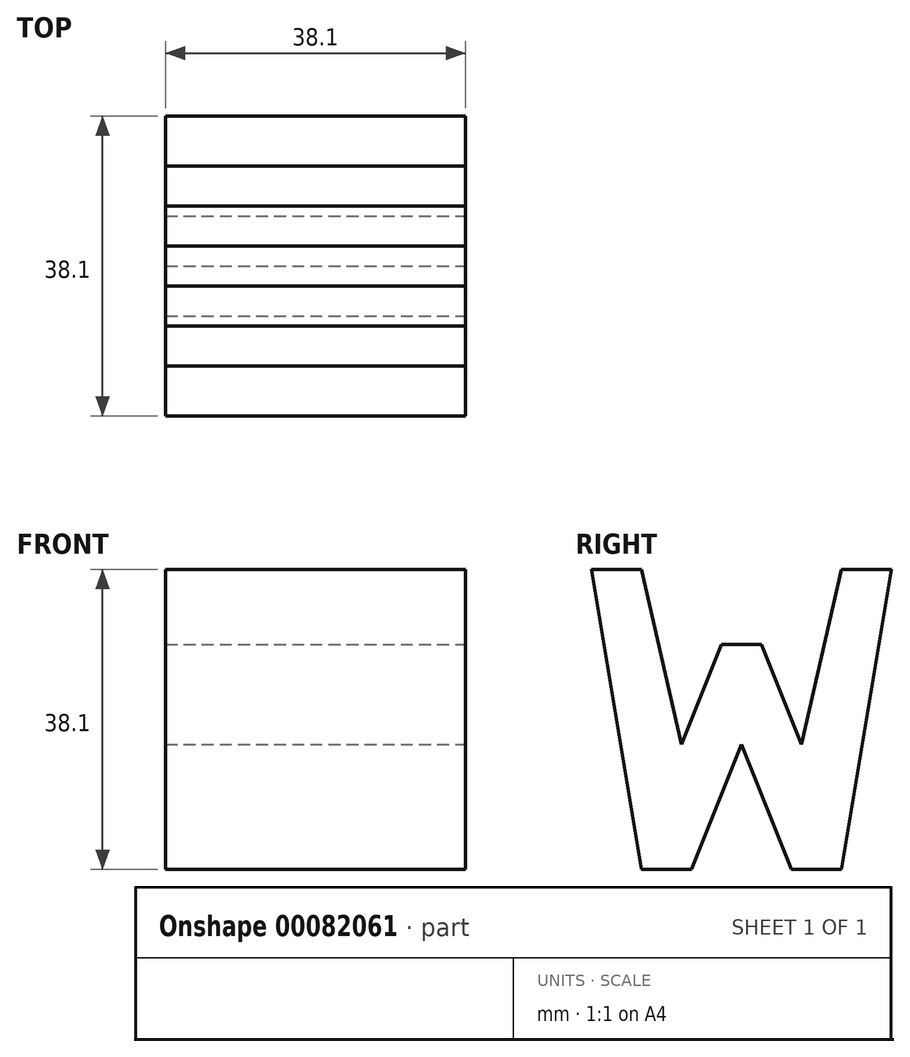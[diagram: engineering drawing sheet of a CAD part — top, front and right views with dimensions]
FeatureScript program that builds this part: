
annotation { "Feature Type Name" : "Feature", "Feature Type Description" : "" }
export const myFeature = defineFeature(function(context is Context, id is Id, definition is map)
    precondition{}
    {
        {
            var Q0;
            Q0=qCreatedBy(makeId("Front.planeOp"),FACE);
            var sketch = newSketch(context, id + "F0", { "sketchPlane" : qUnion([Q0])});
            skLineSegment(sketch, "E0", {"start": v(0, 0) * mm, "end": v(38.1, 0) * mm});
            skLineSegment(sketch, "E1", {"start": v(38.1, 0) * mm, "end": v(38.1, 38.1) * mm});
            skLineSegment(sketch, "E2", {"start": v(38.1, 38.1) * mm, "end": v(0, 38.1) * mm});
            skLineSegment(sketch, "E3", {"start": v(0, 0) * mm, "end": v(0, 38.1) * mm});
            skSolve(sketch);
        }
        {
            var Q0;
            Q0 = qSketchRegion(id + "F0", true);
            extrude(context, id + "F1", {"entities" : qUnion([Q0]), "depth" : 38.1 * mm});
        }
        {
            var Q0;
            Q0=qCreatedBy(makeId("Front.planeOp"),FACE);
            cPlane(context, id + "F2", {"entities" : qUnion([Q0]), "cplaneType" : CPlaneType.OFFSET, "offset" : 38.1 * mm, "width" : 152.4 * mm, "height" : 152.4 * mm});
        }
        {
            var Q0;
            Q0=qCreatedBy(makeId("Right.planeOp"),FACE);
            cPlane(context, id + "F3", {"entities" : qUnion([Q0]), "cplaneType" : CPlaneType.OFFSET, "offset" : 38.1 * mm, "width" : 152.4 * mm, "height" : 152.4 * mm});
        }
        {
            var Q0;
            Q0=qCreatedBy(id+"F3.planeOp",FACE);
            var sketch = newSketch(context, id + "F4", { "sketchPlane" : qUnion([Q0])});
            skLineSegment(sketch, "E4", {"start": v(0, 38.1) * mm, "end": v(-38.1, 38.1) * mm});
            skLineSegment(sketch, "E5", {"start": v(-38.1, 38.1) * mm, "end": v(-38.1, 0) * mm});
            skLineSegment(sketch, "E6", {"start": v(-38.1, 0) * mm, "end": v(0, 0) * mm});
            skLineSegment(sketch, "E7", {"start": v(-38.1, 38.1) * mm, "end": v(-31.75, 0) * mm});
            skLineSegment(sketch, "E8", {"start": v(-25.4, 0) * mm, "end": v(-19.05, 15.88) * mm});
            skLineSegment(sketch, "E9", {"start": v(-19.05, 15.88) * mm, "end": v(-12.7, 0) * mm});
            skLineSegment(sketch, "E10", {"start": v(-12.7, 0) * mm, "end": v(-6.35, 0) * mm});
            skLineSegment(sketch, "E11", {"start": v(-6.35, 0) * mm, "end": v(0, 38.1) * mm});
            skLineSegment(sketch, "E12", {"start": v(-31.75, 38.1) * mm, "end": v(-26.67, 15.88) * mm});
            skLineSegment(sketch, "E13", {"start": v(-26.67, 15.88) * mm, "end": v(-21.59, 28.58) * mm});
            skLineSegment(sketch, "E14", {"start": v(-21.59, 28.58) * mm, "end": v(-16.5, 28.58) * mm});
            skLineSegment(sketch, "E15", {"start": v(-16.5, 28.58) * mm, "end": v(-11.43, 15.88) * mm});
            skLineSegment(sketch, "E16", {"start": v(-11.43, 15.88) * mm, "end": v(-6.35, 38.1) * mm});
            skLineSegment(sketch, "E17", {"start": v(0, 38.1) * mm, "end": v(0, 0) * mm});
            skSolve(sketch);
        }
        {
            var Q0;
            {var subQ0=sQuery(id+"F4.wireOp",EDGE,"E8");Q0=makeQuery(id+"F4.imprint","IMPRINT",FACE,{"disambiguationData":[TD([[makeQuery(id+"F4.imprint","IMPRINT",EDGE,{"derivedFrom":subQ0}),-1.0]])]});}
            var Q1;
            {var subQ0=sQuery(id+"F4.wireOp",EDGE,"E5");Q1=makeQuery(id+"F4.imprint","IMPRINT",FACE,{"disambiguationData":[TD([[makeQuery(id+"F4.imprint","IMPRINT",EDGE,{"derivedFrom":subQ0}),1.0]])]});}
            var Q2;
            {var subQ1=sQuery(id+"F4.wireOp",EDGE,"E12");Q2=makeQuery(id+"F4.imprint","IMPRINT",FACE,{"disambiguationData":[TD([[makeQuery(id+"F4.imprint","IMPRINT",EDGE,{"derivedFrom":subQ1}),1.0]])]});}
            var Q3;
            {var subQ2=sQuery(id+"F4.wireOp",EDGE,"E11");Q3=makeQuery(id+"F4.imprint","IMPRINT",FACE,{"disambiguationData":[TD([[makeQuery(id+"F4.imprint","IMPRINT",EDGE,{"derivedFrom":subQ2}),-1.0]])]});}
            extrude(context, id + "F5", {"entities" : qUnion([Q0, Q1, Q2, Q3]), "operationType" : NewBodyOperationType.REMOVE, "oppositeDirection" : true, "depth" : 38.1 * mm});
        }
    });
